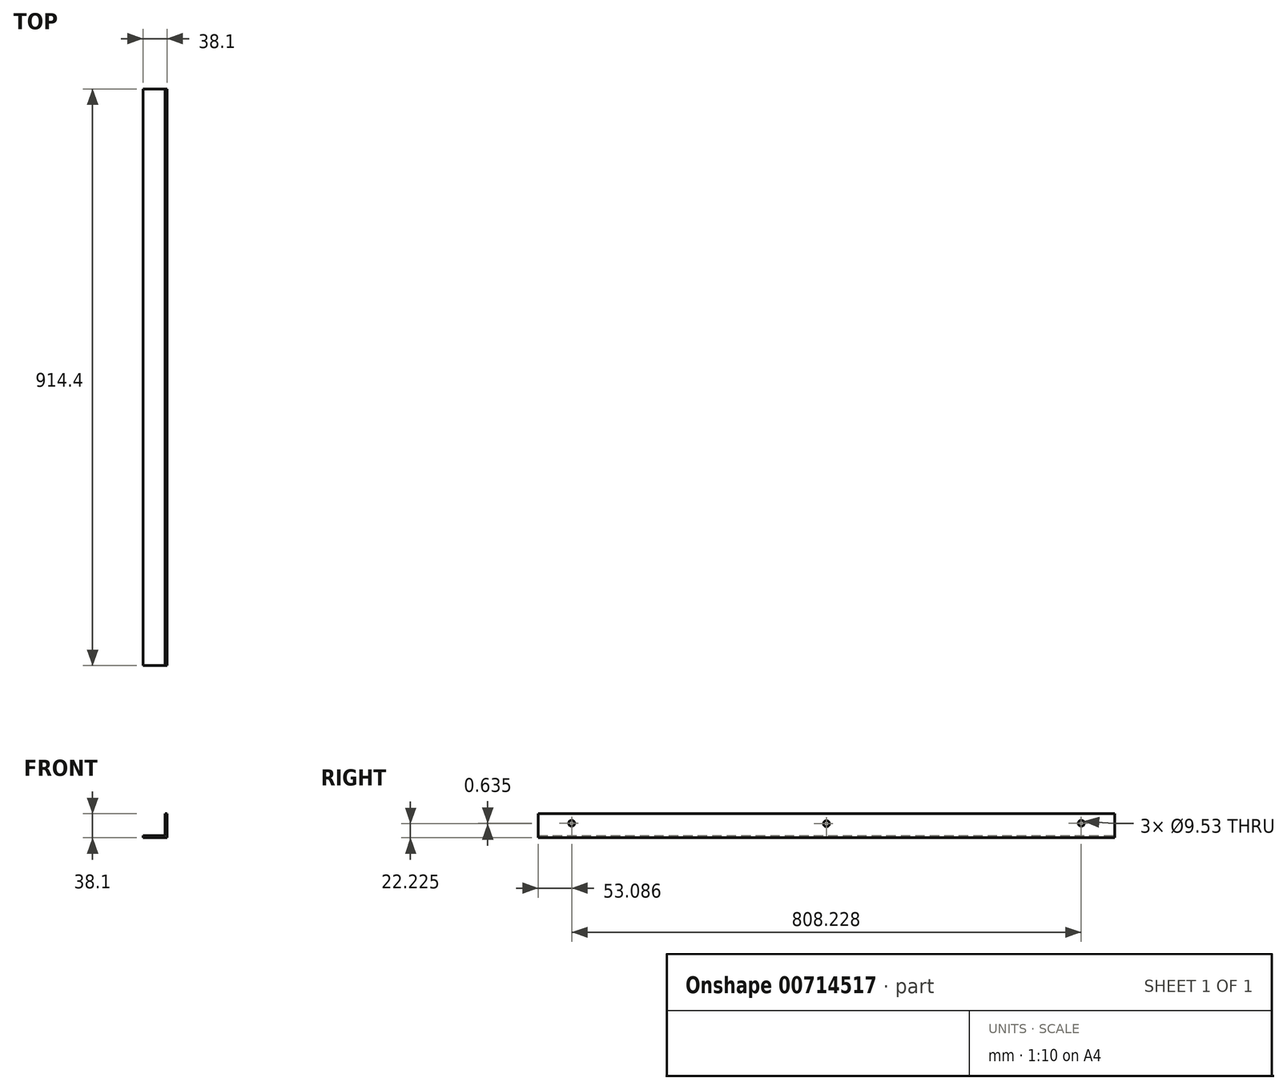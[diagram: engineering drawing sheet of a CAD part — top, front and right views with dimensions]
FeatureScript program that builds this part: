
annotation { "Feature Type Name" : "Feature", "Feature Type Description" : "" }
export const myFeature = defineFeature(function(context is Context, id is Id, definition is map)
    precondition{}
    {
        {
            var Q0;
            Q0=qCreatedBy(makeId("Front.planeOp"),FACE);
            var sketch = newSketch(context, id + "F0", { "sketchPlane" : qUnion([Q0])});
            skLineSegment(sketch, "E0", {"start": v(0, 0) * mm, "end": v(38.1, 0) * mm});
            skLineSegment(sketch, "E1", {"start": v(38.1, 0) * mm, "end": v(38.1, 38.1) * mm});
            skLineSegment(sketch, "E2", {"start": v(38.1, 38.1) * mm, "end": v(34.93, 38.1) * mm});
            skLineSegment(sketch, "E3", {"start": v(34.93, 38.1) * mm, "end": v(34.93, 3.18) * mm});
            skLineSegment(sketch, "E4", {"start": v(34.93, 3.18) * mm, "end": v(0, 3.18) * mm});
            skLineSegment(sketch, "E5", {"start": v(0, 3.18) * mm, "end": v(0, 0) * mm});
            skSolve(sketch);
        }
        {
            var Q0;
            Q0=makeQuery(id+"F0.imprint","IMPRINT",FACE,{"disambiguationData":[TD([[makeQuery(id+"F0.imprint","IMPRINT",EDGE,{"derivedFrom":sQuery(id+"F0.wireOp",EDGE,"E0")}),1.0]])]});
            extrude(context, id + "F1", {"entities" : qUnion([Q0]), "depth" : 914.4 * mm, "offsetDistance" : 25.4 * mm});
        }
        {
            var Q0;
            Q0=makeQuery(id+"F1.opExtrude","SWEPT_FACE",FACE,{"disambiguationData":[OSD([sQuery(id+"F0.wireOp",EDGE,"E1")])]});
            var sketch = newSketch(context, id + "F2", { "sketchPlane" : qUnion([Q0])});
            skCircle(sketch, "E6", {"center": v(-457.2, 22.23) * mm, "radius": 4.76 * mm});
            skCircle(sketch, "E7", {"center": v(-861.31, 22.86) * mm, "radius": 4.76 * mm});
            skCircle(sketch, "E8", {"center": v(-53.09, 22.86) * mm, "radius": 4.76 * mm});
            skSolve(sketch);
        }
        {
            var Q0;
            Q0=makeQuery(id+"F2.imprint","IMPRINT",FACE,{"disambiguationData":[TD([[makeQuery(id+"F2.imprint","IMPRINT",EDGE,{"derivedFrom":sQuery(id+"F2.wireOp",EDGE,"E7")}),1.0]])]});
            var Q1;
            Q1=makeQuery(id+"F2.imprint","IMPRINT",FACE,{"disambiguationData":[TD([[makeQuery(id+"F2.imprint","IMPRINT",EDGE,{"derivedFrom":sQuery(id+"F2.wireOp",EDGE,"E6")}),1.0]])]});
            var Q2;
            Q2=makeQuery(id+"F2.imprint","IMPRINT",FACE,{"disambiguationData":[TD([[makeQuery(id+"F2.imprint","IMPRINT",EDGE,{"derivedFrom":sQuery(id+"F2.wireOp",EDGE,"E8")}),1.0]])]});
            extrude(context, id + "F3", {"entities" : qUnion([Q0, Q1, Q2]), "operationType" : NewBodyOperationType.REMOVE, "endBound" : BoundingType.THROUGH_ALL, "oppositeDirection" : true, "depth" : 25.4 * mm, "offsetDistance" : 25.4 * mm});
        }
    });
